# Revit family: Franke_A200_FM_CM_Tank(EU)
name_source: partatom
category: Specialty Equipment
revit_build: Autodesk Revit 2015 (Build: 20140606_1530(x64)
units: mm (PartAtom-declared; Revit-internal decimal feet)

## types (2) — shared parameters
Assembly Code = fully automatic coffee machine
Cycle (A200) = 50 Hz
Cycle (SU05) = 50 Hz
Cycle Alternative (A200) = 60 Hz
Cycle Alternative (SU05) = 60 Hz
Depth (mm) = 560 mm  [stored 1.83727 ft]
Description = A200 fully automatic coffee machine incl. Refrigerator SU05 FM
Energy loss acc. to DIN 18873(A200 FM incl. SU05 FM) = 1,105 kWh/24h - 230 V
Height (mm) = 604 mm  [stored 1.98163 ft]
Keynote = fully automatic coffee machine
Manufacturer = Franke
Max Overcurrent Protection (A200) = 16 A
Max Overcurrent Protection (SU05) = 10 A
Milk storage (SU05) = 5 l
Model = 410914 - A200 FM CM Tank
Noise emission = 70 dB
Number of Nutral Conductors (A200) = 1
Number of Nutral Conductors (SU05) = 1
Number of Poles (A200) = 1
Number of Poles (SU05) = 1
Number of Protective Conductors (A200) = 1
Number of Protective Conductors (SU05) = 1
Temperature range = + 3° to - 8°
URL = https://www.franke.com
Volts max. (A200) = 240 V
Volts max. (SU05) = 240 V
Volts min. (A200) = 220 V
Volts min. (SU05) = 220 V
Water tank = 4,0 l
Watts max. (A200) = 2750 W
Watts max. (SU05) = 2300 W
Watts min. (A200) = 2400 W
Watts min. (SU05) = 1950 W
Weight = 50 kg
Width (mm) = 613 mm  [stored 2.01115 ft]
zero-valued in all types: Cost

## per-type parameters (varying)
| type | Frontcover |
| A200 FM CM Tank(220-240V/black line/EU) | Franke Black |
| A200 FM CM Tank(220-240V/anthracite/EU) | Franke Anthracite |

note: [stored X ft] marks values corroborated as IEEE doubles in the binary element streams (Revit-internal decimal feet)
